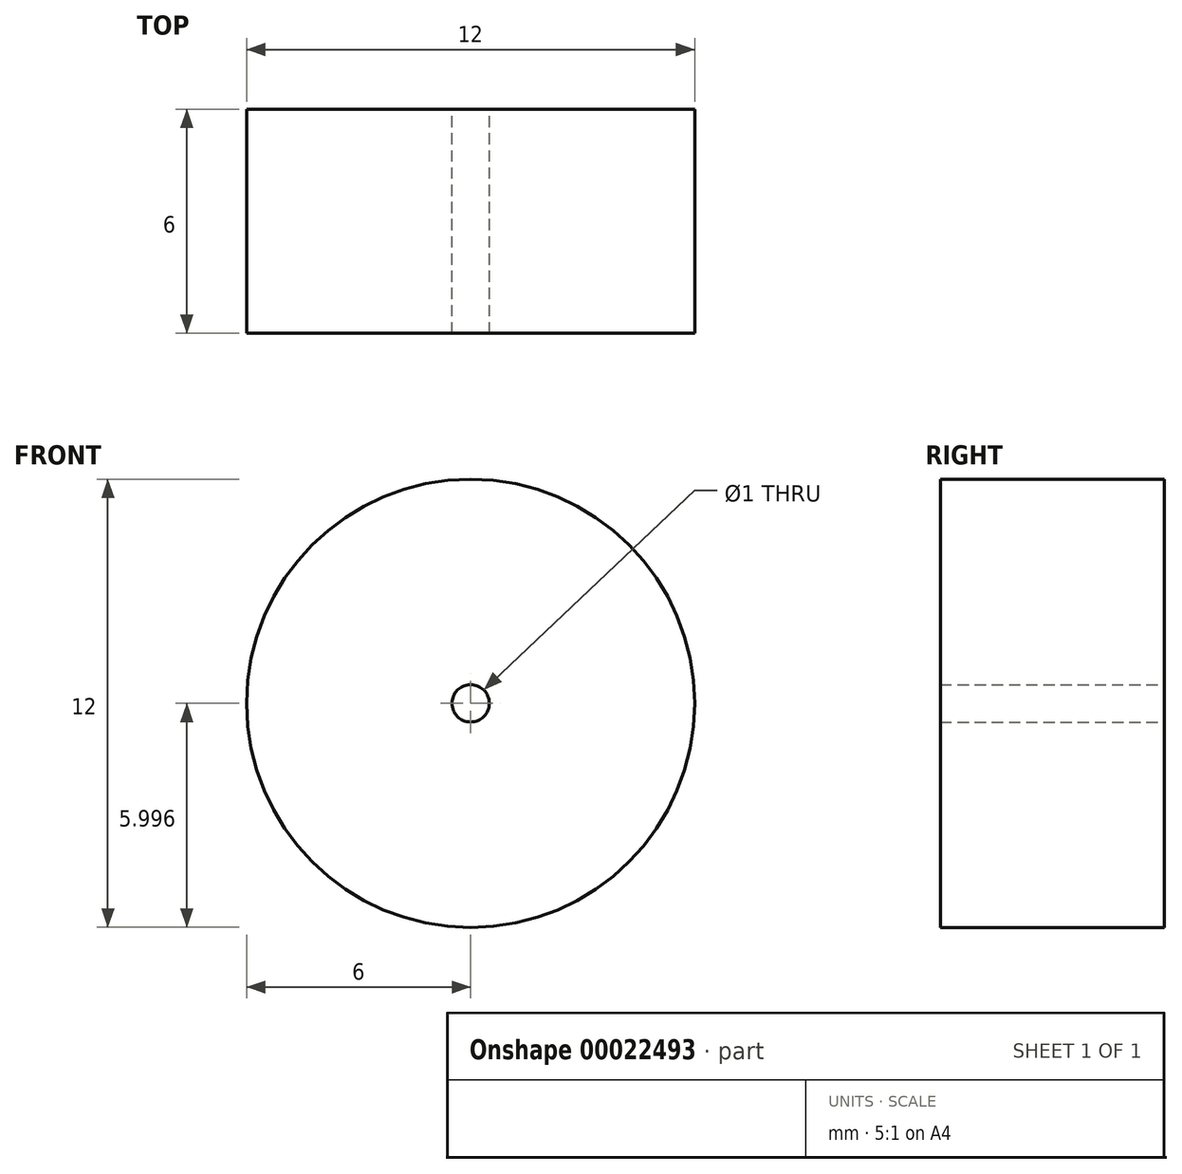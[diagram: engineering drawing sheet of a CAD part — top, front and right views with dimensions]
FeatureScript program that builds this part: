
annotation { "Feature Type Name" : "Feature", "Feature Type Description" : "" }
export const myFeature = defineFeature(function(context is Context, id is Id, definition is map)
    precondition{}
    {
        {
            var Q0;
            Q0=qCreatedBy(makeId("Front.planeOp"),FACE);
            var sketch = newSketch(context, id + "F0", { "sketchPlane" : qUnion([Q0])});
            skCircle(sketch, "E0", {"center": v(-7.45, 33.23) * mm, "radius": 6 * mm});
            skCircle(sketch, "E1", {"center": v(-7.45, 33.23) * mm, "radius": 0.5 * mm});
            skSolve(sketch);
        }
        {
            var Q0;
            Q0=makeQuery(id+"F0.imprint","IMPRINT",FACE,{"disambiguationData":[TD([[makeQuery(id+"F0.imprint","IMPRINT",EDGE,{"derivedFrom":sQuery(id+"F0.wireOp",EDGE,"E0")}),1.0]])]});
            extrude(context, id + "F1", {"entities" : qUnion([Q0]), "depth" : 6 * mm});
        }
    });
